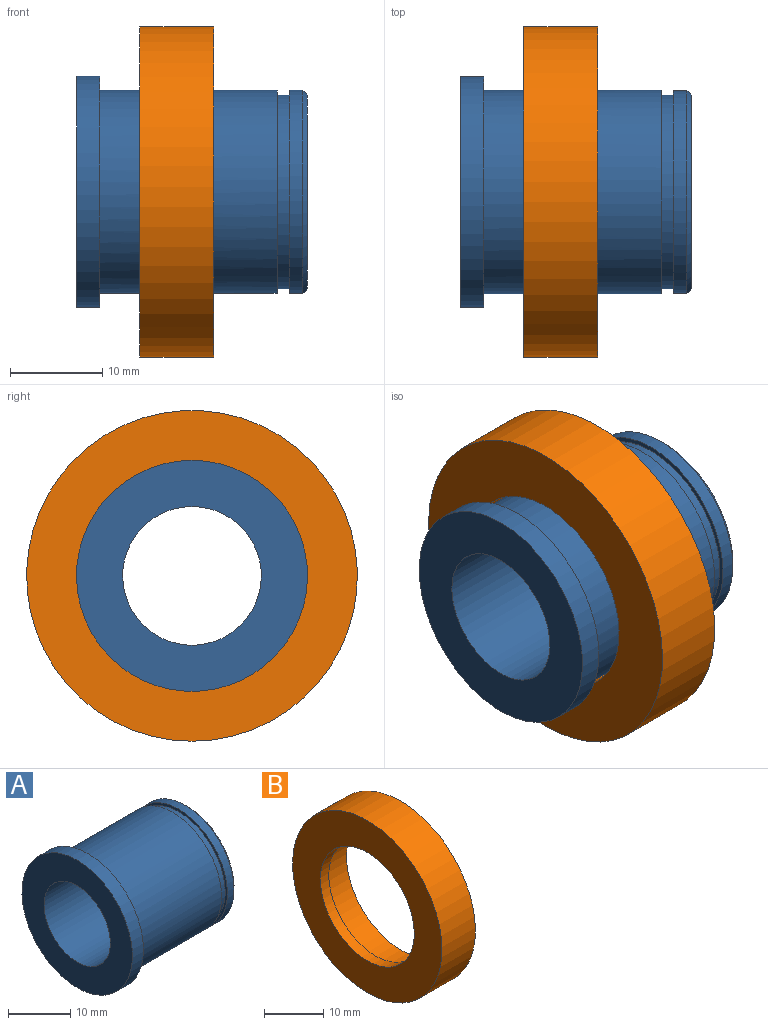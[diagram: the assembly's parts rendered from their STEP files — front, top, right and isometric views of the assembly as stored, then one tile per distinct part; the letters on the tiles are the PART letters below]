
ASSEMBLY  parts=2 mates=1
PART A: 11 faces, bbox 25x25x25 mm
  f0: cylinder r=11mm len=22mm, axis (-1,0,0), area 103.7mm2, adj f7,f10
  f1: plane 25x25mm, normal (-1,0,0), area 314.2mm2, adj f2,f6
  f2: cylinder r=7.5mm len=25mm, axis (-1,0,0), area 1178.1mm2, adj f1,f3
  f3: plane 21x21mm, normal (1,0,0), area 169.6mm2, adj f2,f7
  f4: cylinder r=11mm len=22mm, axis (-1,0,0), area 1327mm2, adj f5,f8
  f5: plane 25x25mm, normal (1,0,0), area 110.7mm2, adj f4,f6
  f6: cylinder r=12.5mm len=25mm, axis (-1,0,0), area 196.3mm2, adj f1,f5
  f7: cone r=11mm half-angle=45deg, axis (-1,0,0), area 47.8mm2, adj f0,f3
  f8: plane 22x22mm, normal (1,0,0), area 33.8mm2, adj f4,f9
  f9: cylinder r=10.5mm len=21mm, axis (1,0,0), area 85.8mm2, adj f8,f10
  f10: plane 22x22mm, normal (-1,0,0), area 33.8mm2, adj f0,f9
PART B: 6 faces, bbox 8x35.8x35.8 mm
  f0: cylinder r=17.9mm len=35.8mm, axis (-1,0,0), area 899.8mm2, adj f1,f2
  f1: plane 35.8x35.8mm, normal (1,0,0), area 475.7mm2, adj f0,f5
  f2: plane 35.8x35.8mm, normal (-1,0,0), area 609mm2, adj f0,f3
  f3: cylinder r=11.25mm len=22.5mm, axis (1,0,0), area 141.4mm2, adj f2,f4
  f4: plane 26x26mm, normal (1,0,0), area 133.3mm2, adj f3,f5
  f5: cylinder r=13mm len=26mm, axis (1,0,0), area 490.1mm2, adj f1,f4
PLACE A t=(-6.66,-3.28,-2.62)mm fixed
PLACE B t=(0.18,-3.28,-2.62)mm
MATE slider B.f3 <-> A.f0  axis (-1,0,0) through (0.18,-3.28,-2.62)mm
